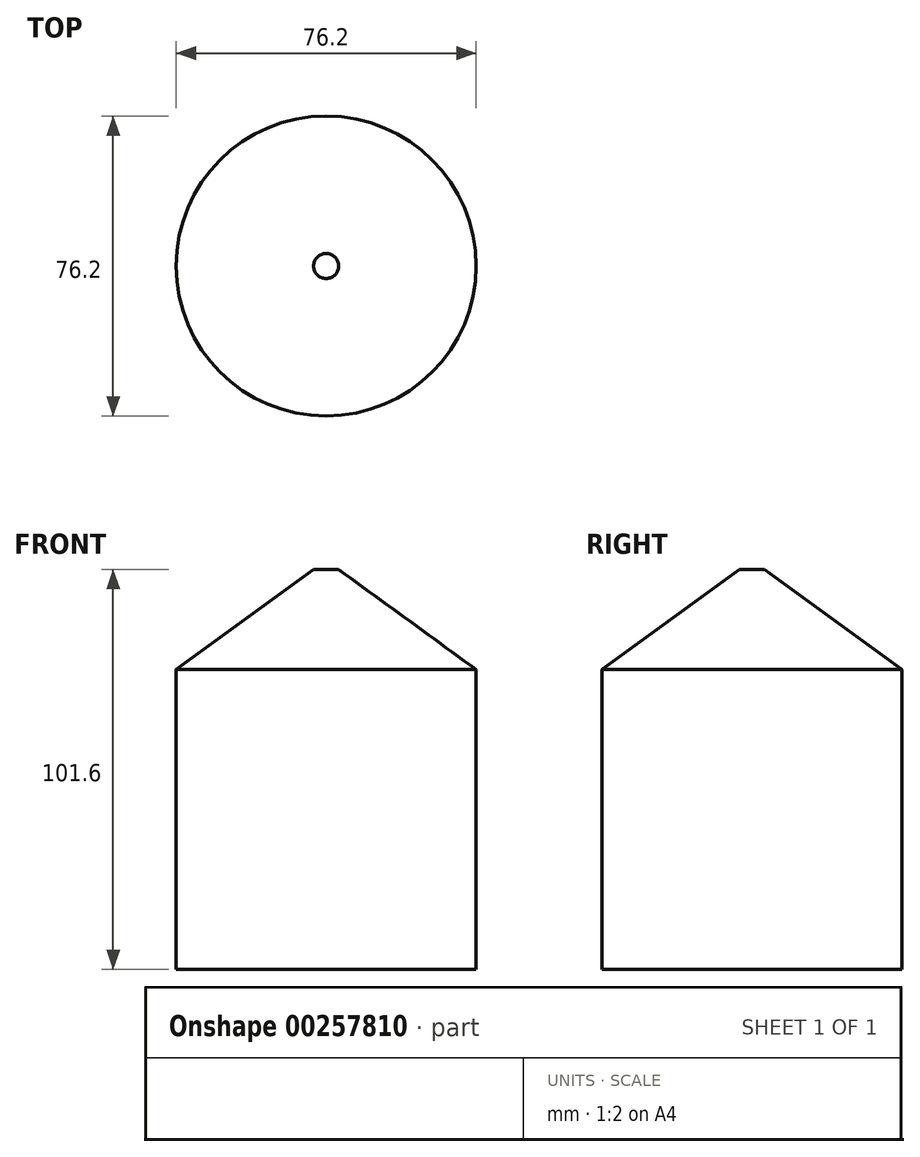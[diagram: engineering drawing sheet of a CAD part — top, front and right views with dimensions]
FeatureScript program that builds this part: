
annotation { "Feature Type Name" : "Feature", "Feature Type Description" : "" }
export const myFeature = defineFeature(function(context is Context, id is Id, definition is map)
    precondition{}
    {
        {
            var Q0;
            Q0=qCreatedBy(makeId("Top.planeOp"),FACE);
            var sketch = newSketch(context, id + "F0", { "sketchPlane" : qUnion([Q0])});
            skCircle(sketch, "E0", {"center": v(0, 0) * mm, "radius": 38.1 * mm});
            skSolve(sketch);
        }
        {
            var Q0;
            Q0 = qSketchRegion(id + "F0", true);
            extrude(context, id + "F1", {"entities" : qUnion([Q0]), "depth" : 76.2 * mm});
        }
        {
            var Q0;
            Q0=makeQuery(id+"F1.opExtrude","CAP_FACE",FACE,{"disambiguationData":[OSD([sQuery(id+"F0.wireOp",EDGE,"E0")])],"isStart":false});
            cPlane(context, id + "F2", {"entities" : qUnion([Q0]), "cplaneType" : CPlaneType.OFFSET, "offset" : 25.4 * mm, "width" : 152.4 * mm, "height" : 152.4 * mm});
        }
        {
            var Q0;
            Q0=qCreatedBy(id+"F2.planeOp",FACE);
            var sketch = newSketch(context, id + "F3", { "sketchPlane" : qUnion([Q0])});
            skCircle(sketch, "E1", {"center": v(0, 0) * mm, "radius": 3.18 * mm});
            skSolve(sketch);
        }
        {
            var Q1;
            Q1=makeQuery(id+"F3.imprint","IMPRINT",FACE,{"disambiguationData":[TD([[makeQuery(id+"F3.imprint","IMPRINT",EDGE,{"derivedFrom":sQuery(id+"F3.wireOp",EDGE,"E1")}),1.0]])]});
            var Q2;
            Q2=makeQuery(id+"F1.opExtrude","CAP_FACE",FACE,{"disambiguationData":[OSD([sQuery(id+"F0.wireOp",EDGE,"E0")])],"isStart":false});
            loft(context, id + "F4", {"operationType" : NewBodyOperationType.ADD, "sheetProfilesArray" : [{ "sheetProfileEntities" : qUnion([Q1]) }, { "sheetProfileEntities" : qUnion([Q2]) }]});
        }
    });
